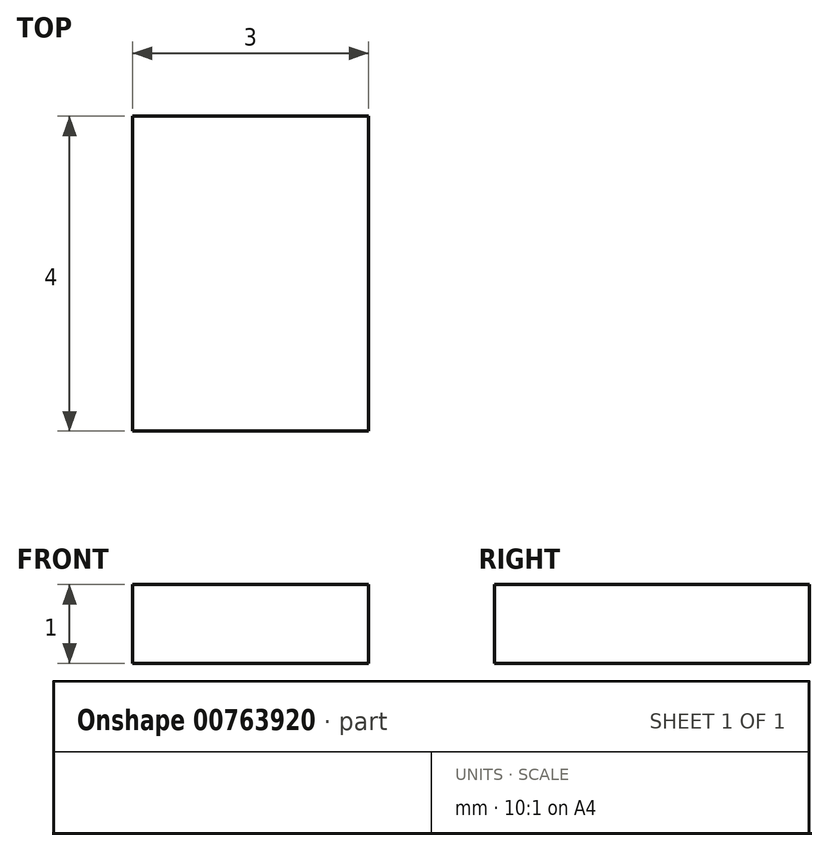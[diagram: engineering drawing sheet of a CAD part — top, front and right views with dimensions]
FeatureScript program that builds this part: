
annotation { "Feature Type Name" : "Feature", "Feature Type Description" : "" }
export const myFeature = defineFeature(function(context is Context, id is Id, definition is map)
    precondition{}
    {
        {
            var Q0;
            Q0=qCreatedBy(makeId("Top.planeOp"),FACE);
            var sketch = newSketch(context, id + "F0", { "sketchPlane" : qUnion([Q0])});
            skLineSegment(sketch, "E0.bottom", {"start": v(1.5, -2) * mm, "end": v(-1.5, -2) * mm});
            skLineSegment(sketch, "E0.top", {"start": v(1.5, 2) * mm, "end": v(-1.5, 2) * mm});
            skLineSegment(sketch, "E0.left", {"start": v(1.5, -2) * mm, "end": v(1.5, 2) * mm});
            skLineSegment(sketch, "E0.right", {"start": v(-1.5, -2) * mm, "end": v(-1.5, 2) * mm});
            skPoint(sketch, "E0.middle", {"position": v(0, 0) * mm});
            skSolve(sketch);
        }
        {
            var Q0;
            Q0=makeQuery(id+"F0.imprint","IMPRINT",FACE,{"disambiguationData":[TD([[makeQuery(id+"F0.imprint","IMPRINT",EDGE,{"derivedFrom":sQuery(id+"F0.wireOp",EDGE,"E0.bottom")}),-1.0]])]});
            extrude(context, id + "F1", {"entities" : qUnion([Q0]), "depth" : 1 * mm, "offsetDistance" : 25.4 * mm});
        }
    });
